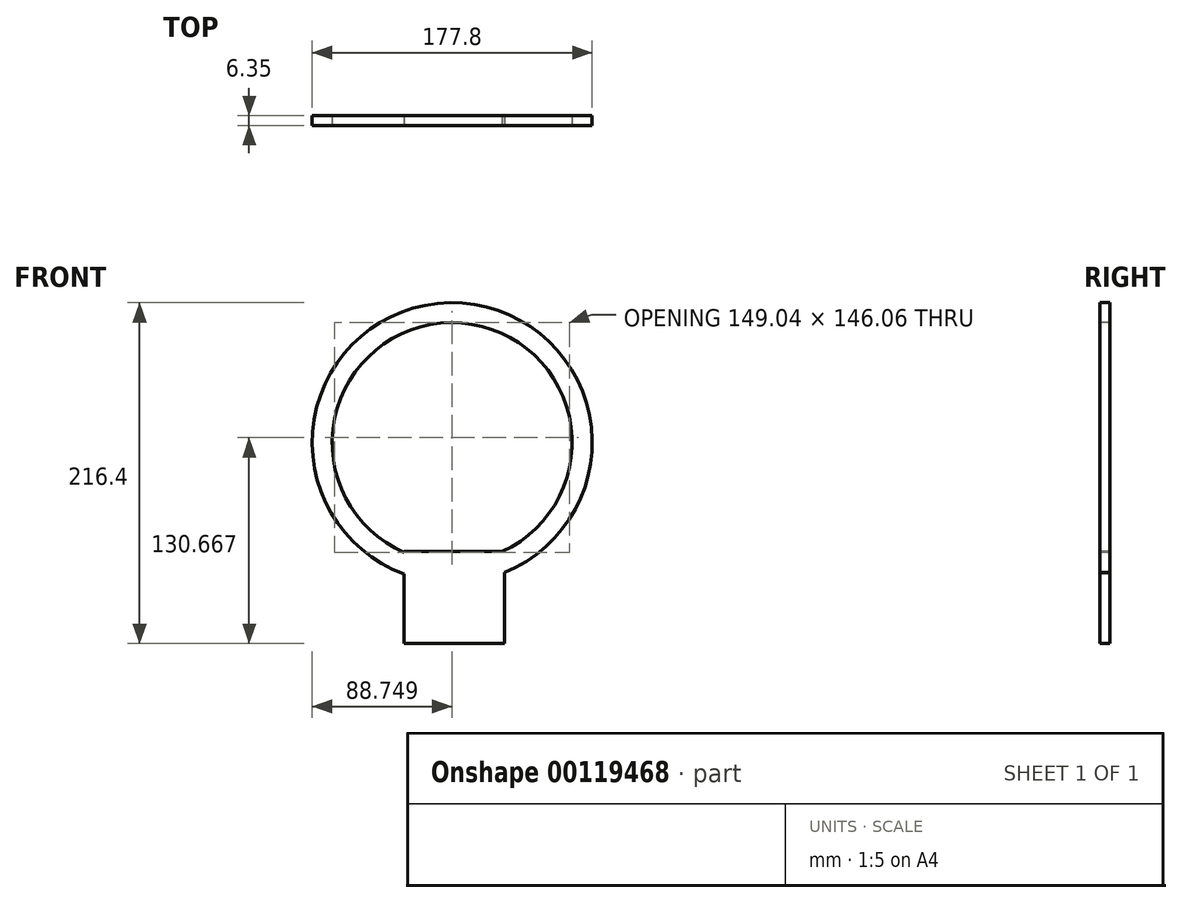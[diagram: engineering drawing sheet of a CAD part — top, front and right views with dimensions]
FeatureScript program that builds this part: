
annotation { "Feature Type Name" : "Feature", "Feature Type Description" : "" }
export const myFeature = defineFeature(function(context is Context, id is Id, definition is map)
    precondition{}
    {
        {
            var Q0;
            Q0=qCreatedBy(makeId("Front.planeOp"),FACE);
            var sketch = newSketch(context, id + "F0", { "sketchPlane" : qUnion([Q0])});
            skCircle(sketch, "E0", {"center": v(0, 0) * mm, "radius": 76.2 * mm});
            skCircle(sketch, "E1", {"center": v(0, 0) * mm, "radius": 88.9 * mm});
            skSolve(sketch);
        }
        {
            var Q0;
            Q0=makeQuery(id+"F0.imprint","IMPRINT",FACE,{"disambiguationData":[TD([[makeQuery(id+"F0.imprint","IMPRINT",EDGE,{"derivedFrom":sQuery(id+"F0.wireOp",EDGE,"E0")}),-1.0]])]});
            extrude(context, id + "F1", {"entities" : qUnion([Q0]), "oppositeDirection" : true, "depth" : 6.35 * mm});
        }
        {
            var Q0;
            Q0=qCreatedBy(makeId("Front.planeOp"),FACE);
            var sketch = newSketch(context, id + "F2", { "sketchPlane" : qUnion([Q0])});
            skLineSegment(sketch, "E2", {"start": v(-30.42, -104.77) * mm, "end": v(-30.42, -127.5) * mm});
            skLineSegment(sketch, "E3", {"start": v(-30.42, -127.5) * mm, "end": v(33.1, -127.5) * mm});
            skLineSegment(sketch, "E4", {"start": v(33.1, -104.4) * mm, "end": v(33.1, -127.5) * mm});
            skLineSegment(sketch, "E5", {"start": v(-30.42, -104.77) * mm, "end": v(-30.4, -84.9) * mm});
            skLineSegment(sketch, "E6", {"start": v(33.1, -104.4) * mm, "end": v(33.1, -84.9) * mm});
            skLineSegment(sketch, "E7", {"start": v(-30.42, -104.77) * mm, "end": v(-30.42, -69.27) * mm});
            skLineSegment(sketch, "E8", {"start": v(33.1, -84.9) * mm, "end": v(33.1, -69.27) * mm});
            skLineSegment(sketch, "E9", {"start": v(33.1, -69.27) * mm, "end": v(-30.42, -69.27) * mm});
            skSolve(sketch);
        }
        {
            var Q0;
            Q0 = qSketchRegion(id + "F2", true);
            extrude(context, id + "F3", {"entities" : qUnion([Q0]), "operationType" : NewBodyOperationType.ADD, "oppositeDirection" : true, "depth" : 6.35 * mm});
        }
    });
